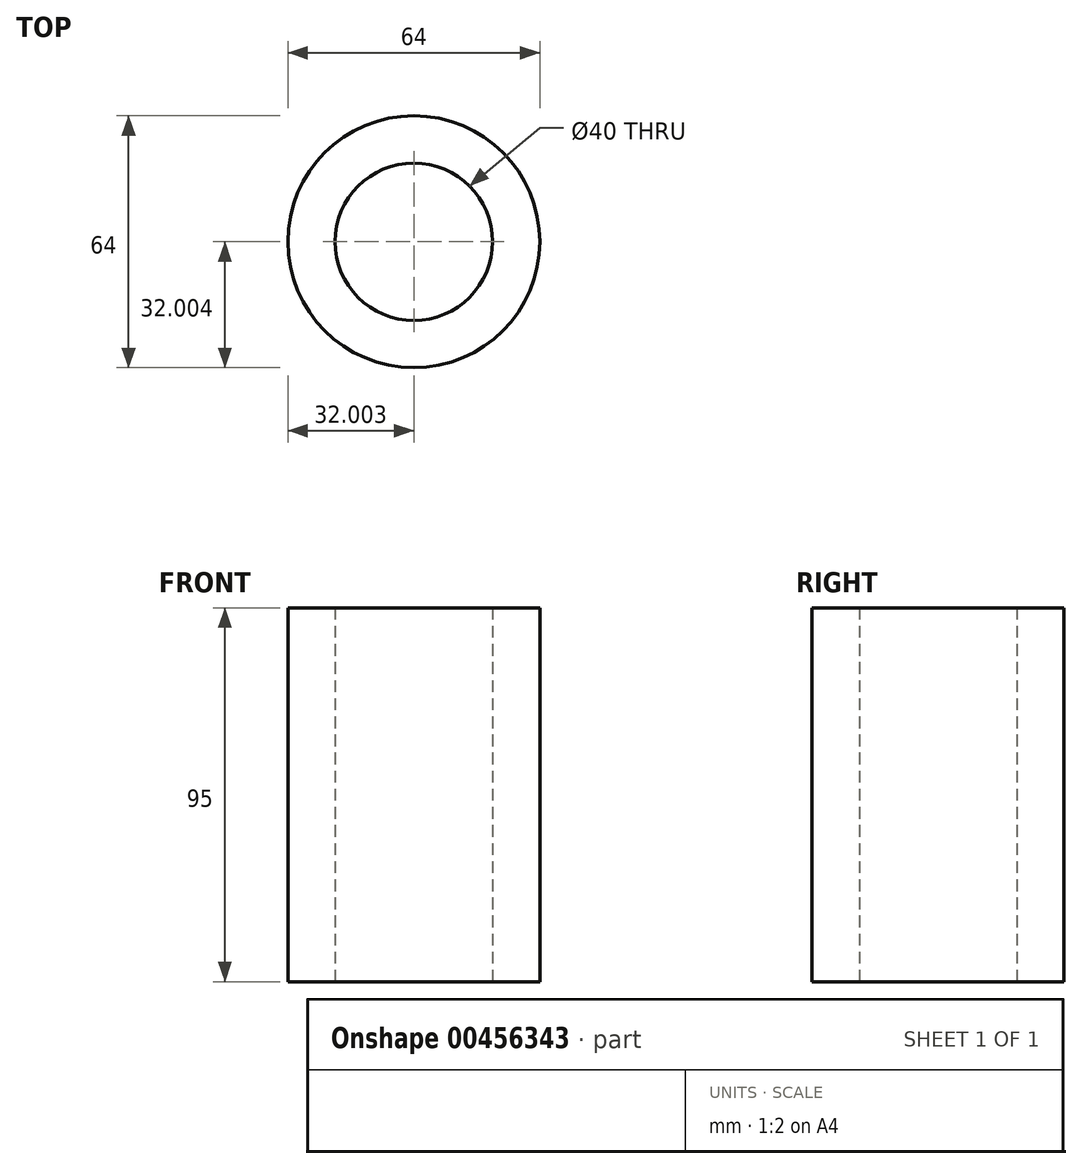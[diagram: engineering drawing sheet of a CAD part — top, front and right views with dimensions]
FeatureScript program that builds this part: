
annotation { "Feature Type Name" : "Feature", "Feature Type Description" : "" }
export const myFeature = defineFeature(function(context is Context, id is Id, definition is map)
    precondition{}
    {
        {
            var Q0;
            Q0=qCreatedBy(makeId("Top.planeOp"),FACE);
            var sketch = newSketch(context, id + "F0", { "sketchPlane" : qUnion([Q0])});
            skCircle(sketch, "E0", {"center": v(-37.47, 40.36) * mm, "radius": 32 * mm});
            skCircle(sketch, "E1", {"center": v(-37.47, 40.36) * mm, "radius": 20 * mm});
            skSolve(sketch);
        }
        {
            var Q0;
            Q0 = qSketchRegion(id + "F0", true);
            extrude(context, id + "F1", {"entities" : qUnion([Q0]), "depth" : 95 * mm});
        }
    });
